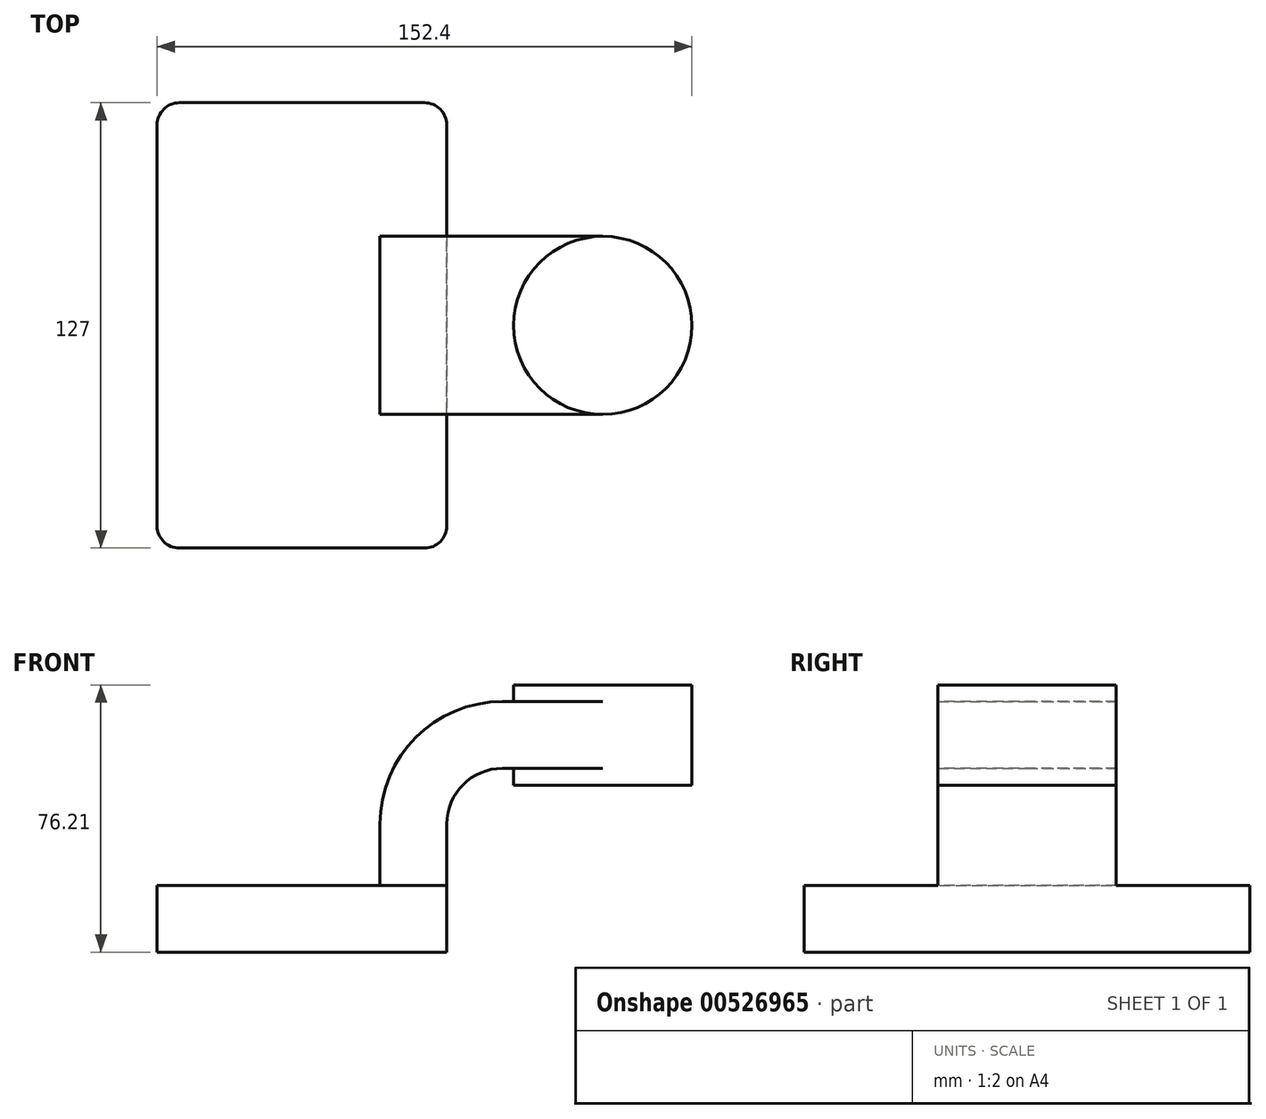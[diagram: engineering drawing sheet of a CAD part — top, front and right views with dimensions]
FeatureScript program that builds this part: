
annotation { "Feature Type Name" : "Feature", "Feature Type Description" : "" }
export const myFeature = defineFeature(function(context is Context, id is Id, definition is map)
    precondition{}
    {
        {
            var Q0;
            Q0=qCreatedBy(makeId("Front.planeOp"),FACE);
            var sketch = newSketch(context, id + "F0", { "sketchPlane" : qUnion([Q0])});
            skLineSegment(sketch, "E0.bottom", {"start": v(41.28, -9.52) * mm, "end": v(-41.28, -9.53) * mm});
            skLineSegment(sketch, "E0.top", {"start": v(41.28, 9.53) * mm, "end": v(-41.28, 9.53) * mm});
            skLineSegment(sketch, "E0.left", {"start": v(41.28, -9.52) * mm, "end": v(41.28, 9.53) * mm});
            skLineSegment(sketch, "E0.right", {"start": v(-41.28, -9.53) * mm, "end": v(-41.28, 9.53) * mm});
            skPoint(sketch, "E0.middle", {"position": v(0, 0) * mm});
            skLineSegment(sketch, "E1.bottom", {"start": v(111.12, 38.1) * mm, "end": v(60.33, 38.1) * mm});
            skLineSegment(sketch, "E1.top", {"start": v(111.12, 66.68) * mm, "end": v(60.33, 66.68) * mm});
            skLineSegment(sketch, "E1.left", {"start": v(111.12, 38.1) * mm, "end": v(111.12, 66.68) * mm});
            skLineSegment(sketch, "E1.right", {"start": v(60.33, 38.1) * mm, "end": v(60.33, 66.68) * mm});
            skPoint(sketch, "E1.middle", {"position": v(85.72, 52.39) * mm});
            skLineSegment(sketch, "E2", {"start": v(41.28, 9.53) * mm, "end": v(41.28, 27) * mm});
            skArc(sketch, "E3", {"start": v(41.27, 27) * mm, "mid": v(45.92, 38.23) * mm, "end": v(57.15, 42.88) * mm});
            skLineSegment(sketch, "E4", {"start": v(57.15, 42.88) * mm, "end": v(85.72, 42.88) * mm});
            skLineSegment(sketch, "E5.0", {"start": v(57.15, 61.93) * mm, "end": v(85.72, 61.93) * mm});
            skArc(sketch, "E5.1", {"start": v(22.23, 27) * mm, "mid": v(32.45, 51.7) * mm, "end": v(57.15, 61.93) * mm});
            skLineSegment(sketch, "E5.2", {"start": v(22.22, 9.53) * mm, "end": v(22.22, 27) * mm});
            skLineSegment(sketch, "E6", {"start": v(85.72, 38.1) * mm, "end": v(85.72, 66.68) * mm});
            skFitSpline(sketch, "E7", {"points": [v(-41.28, 9.53) * mm, v(57.15, 61.93) * mm], "startDerivative": vector(11.92, 85.12) * mm, "endDerivative": vector(133.43, -18.05) * mm});
            skSolve(sketch);
        }
        {
            var Q0;
            Q0=makeQuery(id+"F0.imprint","IMPRINT",FACE,{"disambiguationData":[TD([[makeQuery(id+"F0.imprint","IMPRINT",EDGE,{"derivedFrom":sQuery(id+"F0.wireOp",EDGE,"E0.bottom")}),-1.0]])]});
            extrude(context, id + "F1", {"entities" : qUnion([Q0]), "endBound" : BoundingType.SYMMETRIC, "depth" : 127 * mm, "offsetDistance" : 25.4 * mm});
        }
        {
            var Q0;
            {var subQ0=sQuery(id+"F0.wireOp",EDGE,"E4");var subQ1=sQuery(id+"F0.wireOp",EDGE,"E1.right");var subQ2=makeQuery(id+"F0.imprint","INTERSECT",VERTEX,{"derivedFrom":[subQ1,subQ0]});Q0=makeQuery(id+"F0.imprint","IMPRINT",FACE,{"disambiguationData":[TD([[makeQuery(id+"F0.imprint","IMPRINT",EDGE,{"disambiguationData":[TD([[subQ2,-1.0]])],"derivedFrom":subQ1}),-1.0]])]});}
            var Q1;
            {var subQ1=sQuery(id+"F0.wireOp",EDGE,"E2");Q1=makeQuery(id+"F0.imprint","IMPRINT",FACE,{"disambiguationData":[TD([[makeQuery(id+"F0.imprint","IMPRINT",EDGE,{"derivedFrom":subQ1}),1.0]])]});}
            extrude(context, id + "F2", {"entities" : qUnion([Q0, Q1]), "operationType" : NewBodyOperationType.ADD, "endBound" : BoundingType.SYMMETRIC, "oppositeDirection" : true, "depth" : 50.8 * mm, "offsetDistance" : 25.4 * mm});
        }
        {
            var Q0;
            Q0=makeQuery(id+"F0.imprint","IMPRINT",FACE,{"disambiguationData":[TD([[makeQuery(id+"F0.imprint","IMPRINT",EDGE,{"derivedFrom":sQuery(id+"F0.wireOp",EDGE,"E5.1")}),1.0]])]});
            extrude(context, id + "F3", {"entities" : qUnion([Q0]), "operationType" : NewBodyOperationType.ADD, "endBound" : BoundingType.SYMMETRIC, "depth" : 15.88 * mm, "offsetDistance" : 25.4 * mm});
        }
        {
            var Q0;
            {var subQ4=sQuery(id+"F0.wireOp",EDGE,"E1.left");Q0=makeQuery(id+"F0.imprint","IMPRINT",FACE,{"disambiguationData":[TD([[makeQuery(id+"F0.imprint","IMPRINT",EDGE,{"derivedFrom":subQ4}),1.0]])]});}
            var Q1;
            Q1=sQuery(id+"F0.wireOp",EDGE,"E6");
            revolve(context, id + "F4", {"operationType" : NewBodyOperationType.ADD, "entities" : qUnion([Q0]), "axis" : qUnion([Q1]), "revolveType" : RevolveType.FULL});
        }
        {
            var Q0;
            Q0=makeQuery(id+"F1.opExtrude","CAP_EDGE",EDGE,{"disambiguationData":[OSD([sQuery(id+"F0.wireOp",EDGE,"E0.right")])],"isStart":false});
            var Q1;
            Q1=makeQuery(id+"F1.opExtrude","CAP_EDGE",EDGE,{"disambiguationData":[OSD([sQuery(id+"F0.wireOp",EDGE,"E0.left")])],"isStart":false});
            var Q2;
            Q2=makeQuery(id+"F1.opExtrude","CAP_EDGE",EDGE,{"disambiguationData":[OSD([sQuery(id+"F0.wireOp",EDGE,"E0.left")])],"isStart":true});
            var Q3;
            Q3=makeQuery(id+"F1.opExtrude","CAP_EDGE",EDGE,{"disambiguationData":[OSD([sQuery(id+"F0.wireOp",EDGE,"E0.right")])],"isStart":true});
            fillet(context, id + "F5", {"entities" : qUnion([Q0, Q1, Q2, Q3]), "radius" : 6.35 * mm, "tangentPropagation" : true, "allowEdgeOverflow" : false});
        }
    });
